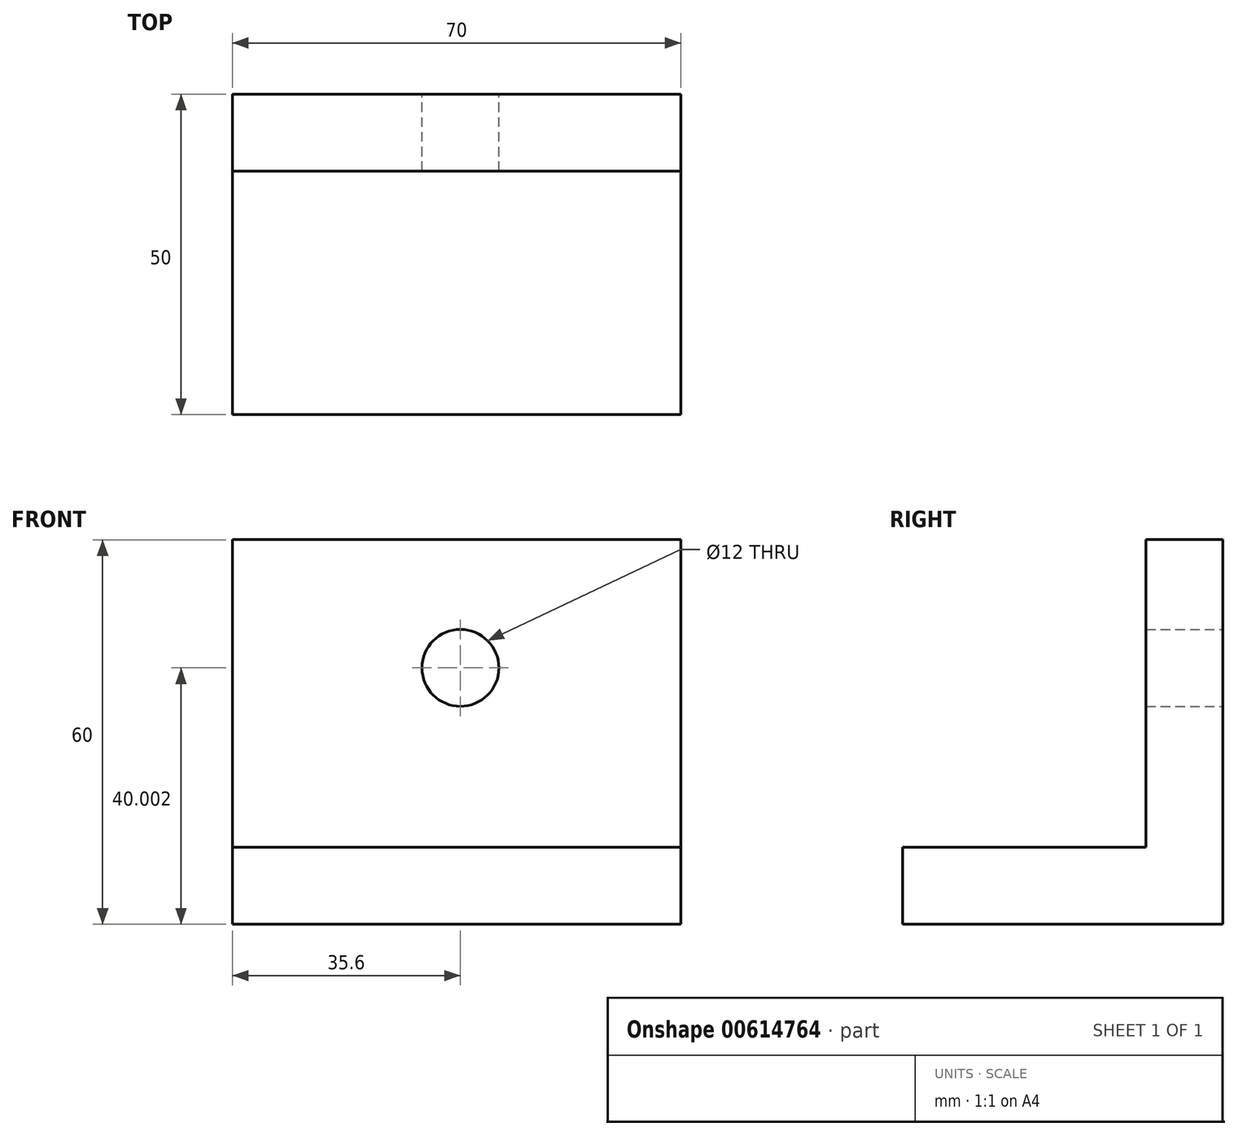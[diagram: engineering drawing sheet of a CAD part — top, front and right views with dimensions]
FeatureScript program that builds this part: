
annotation { "Feature Type Name" : "Feature", "Feature Type Description" : "" }
export const myFeature = defineFeature(function(context is Context, id is Id, definition is map)
    precondition{}
    {
        {
            var Q0;
            Q0=qCreatedBy(makeId("Front.planeOp"),FACE);
            var sketch = newSketch(context, id + "F0", { "sketchPlane" : qUnion([Q0])});
            skLineSegment(sketch, "E0.bottom", {"start": v(-35.6, 37) * mm, "end": v(34.4, 37) * mm});
            skLineSegment(sketch, "E0.top", {"start": v(-35.6, -23) * mm, "end": v(34.4, -23) * mm});
            skLineSegment(sketch, "E0.left", {"start": v(-35.6, 37) * mm, "end": v(-35.6, -23) * mm});
            skLineSegment(sketch, "E0.right", {"start": v(34.4, 37) * mm, "end": v(34.4, -23) * mm});
            skLineSegment(sketch, "E1.top", {"start": v(-35.6, -11) * mm, "end": v(34.4, -11) * mm});
            skLineSegment(sketch, "E1.left", {"start": v(-35.6, -23) * mm, "end": v(-35.6, -11) * mm});
            skLineSegment(sketch, "E1.right", {"start": v(34.4, -23) * mm, "end": v(34.4, -11) * mm});
            skLineSegment(sketch, "E2.bottom", {"start": v(-35.6, 37) * mm, "end": v(0, 37) * mm});
            skLineSegment(sketch, "E2.top", {"start": v(-35.6, 37) * mm, "end": v(0, 37) * mm});
            skLineSegment(sketch, "E2.left", {"start": v(-35.6, 37) * mm, "end": v(-35.6, 37) * mm});
            skLineSegment(sketch, "E2.right", {"start": v(0, 37) * mm, "end": v(0, 37) * mm});
            skLineSegment(sketch, "E3", {"start": v(0, 37) * mm, "end": v(0, 17) * mm});
            skCircle(sketch, "E4", {"center": v(0, 17) * mm, "radius": 6 * mm});
            skSolve(sketch);
        }
        {
            var Q0;
            Q0=makeQuery(id+"F0.imprint","IMPRINT",FACE,{"disambiguationData":[TD([[makeQuery(id+"F0.imprint","IMPRINT",EDGE,{"derivedFrom":sQuery(id+"F0.wireOp",EDGE,"E0.top")}),1.0]])]});
            extrude(context, id + "F1", {"entities" : qUnion([Q0]), "depth" : 50 * mm, "offsetDistance" : 25 * mm});
        }
        {
            var Q0;
            Q0 = qSketchRegion(id + "F0", true);
            extrude(context, id + "F2", {"entities" : qUnion([Q0]), "operationType" : NewBodyOperationType.ADD, "depth" : 12 * mm, "offsetDistance" : 25 * mm});
        }
    });
